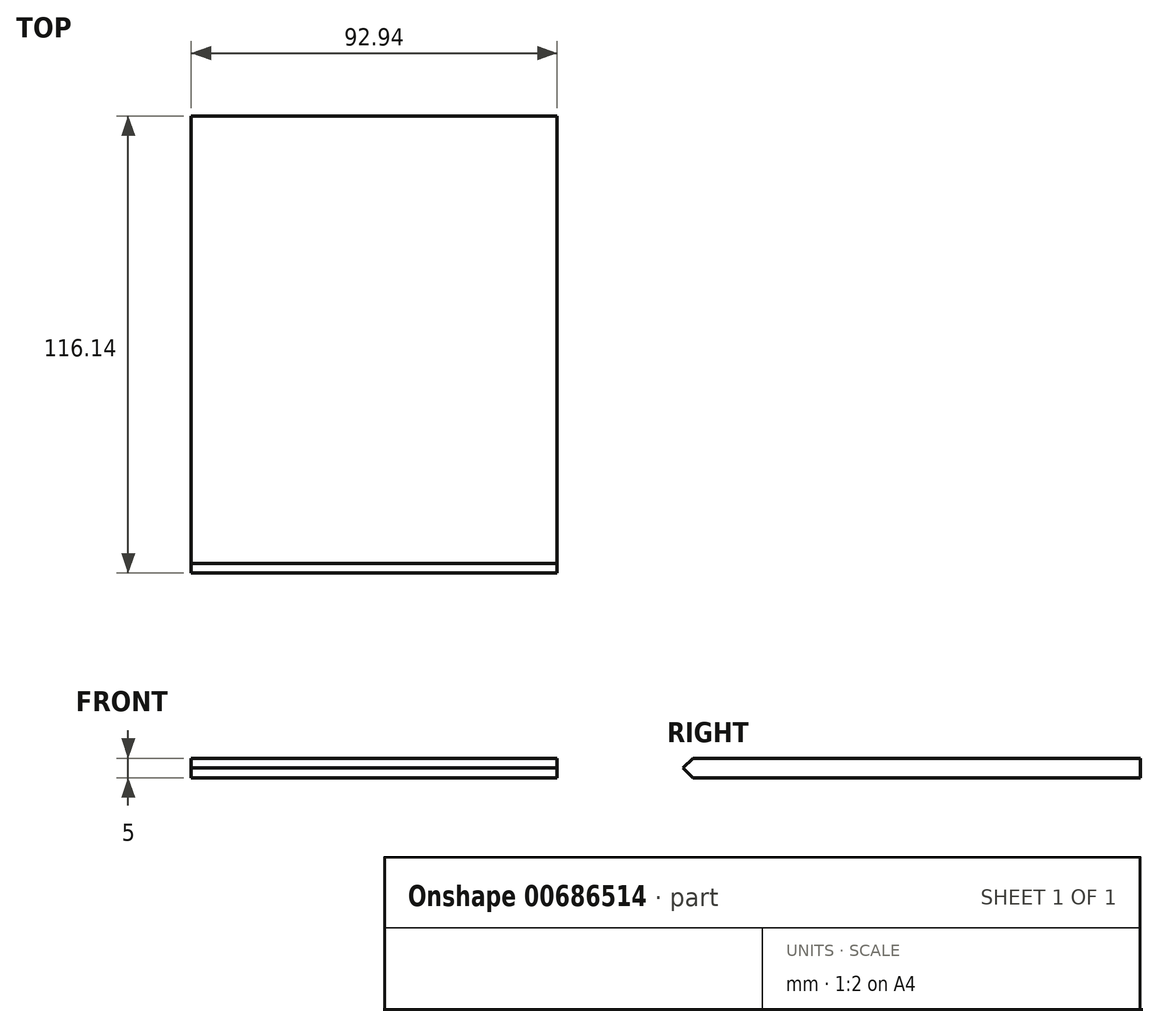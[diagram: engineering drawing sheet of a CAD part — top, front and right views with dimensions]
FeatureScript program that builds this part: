
annotation { "Feature Type Name" : "Feature", "Feature Type Description" : "" }
export const myFeature = defineFeature(function(context is Context, id is Id, definition is map)
    precondition{}
    {
        {
            var Q0;
            Q0=qCreatedBy(makeId("Top.planeOp"),FACE);
            var sketch = newSketch(context, id + "F0", { "sketchPlane" : qUnion([Q0])});
            skLineSegment(sketch, "E0.bottom", {"start": v(-35.67, 42.7) * mm, "end": v(35.67, 42.7) * mm});
            skLineSegment(sketch, "E0.top", {"start": v(-35.67, -42.7) * mm, "end": v(35.67, -42.7) * mm});
            skLineSegment(sketch, "E0.left", {"start": v(-35.67, 42.7) * mm, "end": v(-35.67, -42.7) * mm});
            skLineSegment(sketch, "E0.right", {"start": v(35.67, 42.7) * mm, "end": v(35.67, -42.7) * mm});
            skPoint(sketch, "E0.middle", {"position": v(0, 0) * mm});
            skSolve(sketch);
        }
        {
            var Q0;
            Q0=makeQuery(id+"F0.imprint","IMPRINT",FACE,{"disambiguationData":[TD([[makeQuery(id+"F0.imprint","IMPRINT",EDGE,{"derivedFrom":sQuery(id+"F0.wireOp",EDGE,"E0.bottom")}),-1.0]])]});
            var sketch = newSketch(context, id + "F1", { "sketchPlane" : qUnion([Q0])});
            skLineSegment(sketch, "E1.bottom", {"start": v(-46.47, 58.07) * mm, "end": v(46.47, 58.07) * mm});
            skLineSegment(sketch, "E1.top", {"start": v(-46.47, -58.07) * mm, "end": v(46.47, -58.07) * mm});
            skLineSegment(sketch, "E1.left", {"start": v(-46.47, 58.07) * mm, "end": v(-46.47, -58.07) * mm});
            skLineSegment(sketch, "E1.right", {"start": v(46.47, 58.07) * mm, "end": v(46.47, -58.07) * mm});
            skPoint(sketch, "E1.middle", {"position": v(0, 0) * mm});
            skSolve(sketch);
        }
        {
            var Q0;
            Q0 = qSketchRegion(id + "F1", true);
            extrude(context, id + "F2", {"entities" : qUnion([Q0]), "depth" : 2.5 * mm, "offsetDistance" : 25 * mm, "hasSecondDirection" : true, "secondDirectionOppositeDirection" : true, "secondDirectionDepth" : 2.5 * mm});
        }
        {
            var Q0;
            Q0=makeQuery(id+"F2.opExtrude","CAP_EDGE",EDGE,{"disambiguationData":[OSD([sQuery(id+"F1.wireOp",EDGE,"E1.top")])],"isStart":false});
            var Q1;
            Q1=makeQuery(id+"F2.opExtrude","CAP_EDGE",EDGE,{"disambiguationData":[OSD([sQuery(id+"F1.wireOp",EDGE,"E1.top")])],"isStart":true});
            chamfer(context, id + "F3", {"entities" : qUnion([Q0, Q1]), "width" : 2.5 * mm, "tangentPropagation" : true});
        }
        {
            var Q0;
            Q0 = qSketchRegion(id + "F0", true);
            extrude(context, id + "F4", {"entities" : qUnion([Q0]), "operationType" : NewBodyOperationType.ADD, "depth" : 1 * mm, "offsetDistance" : 25 * mm, "hasSecondDirection" : true, "secondDirectionOppositeDirection" : true, "secondDirectionDepth" : 1 * mm});
        }
    });
